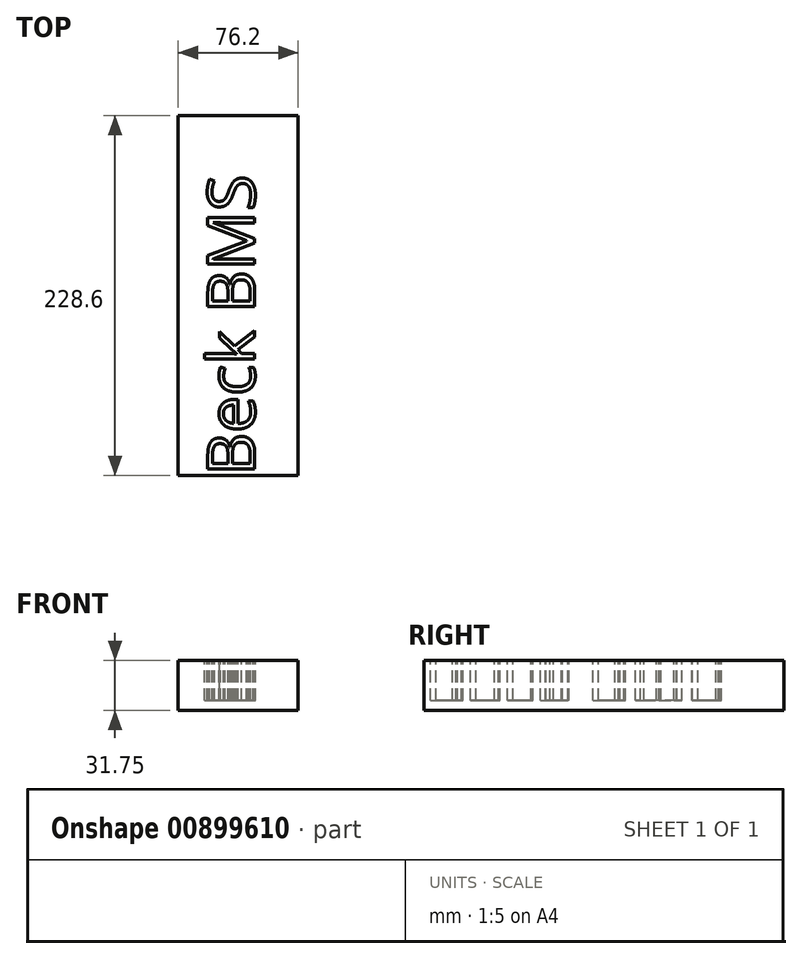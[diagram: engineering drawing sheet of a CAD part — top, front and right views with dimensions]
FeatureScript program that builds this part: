
annotation { "Feature Type Name" : "Feature", "Feature Type Description" : "" }
export const myFeature = defineFeature(function(context is Context, id is Id, definition is map)
    precondition{}
    {
        {
            var Q0;
            Q0=qCreatedBy(makeId("Top.planeOp"),FACE);
            var sketch = newSketch(context, id + "F0", { "sketchPlane" : qUnion([Q0])});
            skLineSegment(sketch, "E0.bottom", {"start": v(0, 0) * mm, "end": v(76.2, 0) * mm});
            skLineSegment(sketch, "E0.top", {"start": v(0, 228.6) * mm, "end": v(76.2, 228.6) * mm});
            skLineSegment(sketch, "E0.left", {"start": v(0, 0) * mm, "end": v(0, 228.6) * mm});
            skLineSegment(sketch, "E0.right", {"start": v(76.2, 0) * mm, "end": v(76.2, 228.6) * mm});
            skSolve(sketch);
        }
        {
            var Q0;
            Q0 = qSketchRegion(id + "F0", true);
            extrude(context, id + "F1", {"entities" : qUnion([Q0]), "depth" : 31.75 * mm, "offsetDistance" : 25.4 * mm});
        }
        {
            var Q0;
            Q0=makeQuery(id+"F1.opExtrude","CAP_FACE",FACE,{"disambiguationData":[OSD([sQuery(id+"F0.wireOp",EDGE,"E0.bottom"),sQuery(id+"F0.wireOp",EDGE,"E0.top"),sQuery(id+"F0.wireOp",EDGE,"E0.left"),sQuery(id+"F0.wireOp",EDGE,"E0.right")])],"isStart":false});
            var sketch = newSketch(context, id + "F2", { "sketchPlane" : qUnion([Q0])});
            skText(sketch, "E1", { "text": "Beck BMS", "fontName": "OpenSans-Regular.ttf"});
            const initialGuessF2  = {"E1": [0.04863, 0, 0, 1, 0.03008]};
            skSetInitialGuess(sketch, initialGuessF2);
            skSolve(sketch);
        }
        {
            var Q0;
            Q0 = qSketchRegion(id + "F2", true);
            extrude(context, id + "F3", {"entities" : qUnion([Q0]), "operationType" : NewBodyOperationType.REMOVE, "oppositeDirection" : true, "depth" : 25.4 * mm, "offsetDistance" : 25.4 * mm});
        }
    });
